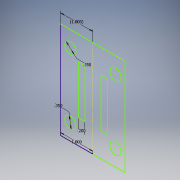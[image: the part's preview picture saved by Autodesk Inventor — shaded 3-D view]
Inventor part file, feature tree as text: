
AUTODESK INVENTOR PART (.ipt)
format: ipt  version: 2017 (Build 210142000, 142)  size: 98,304 bytes
history: native  units: in
note: dims shown in document units (in); Inventor stores cm internally (conversion verified against a paired STEP export)
features: sketch x1
ambient origin geometry x8: Origin, YZ Plane, XZ Plane, XY Plane, X Axis, Y Axis, Z Axis, Center Point
feature tree (1):
  sketch  "Sketch1"  dims[d0=1.0in d2=1.0in d6=0.2in d10=0.35in d11=0.35in]
